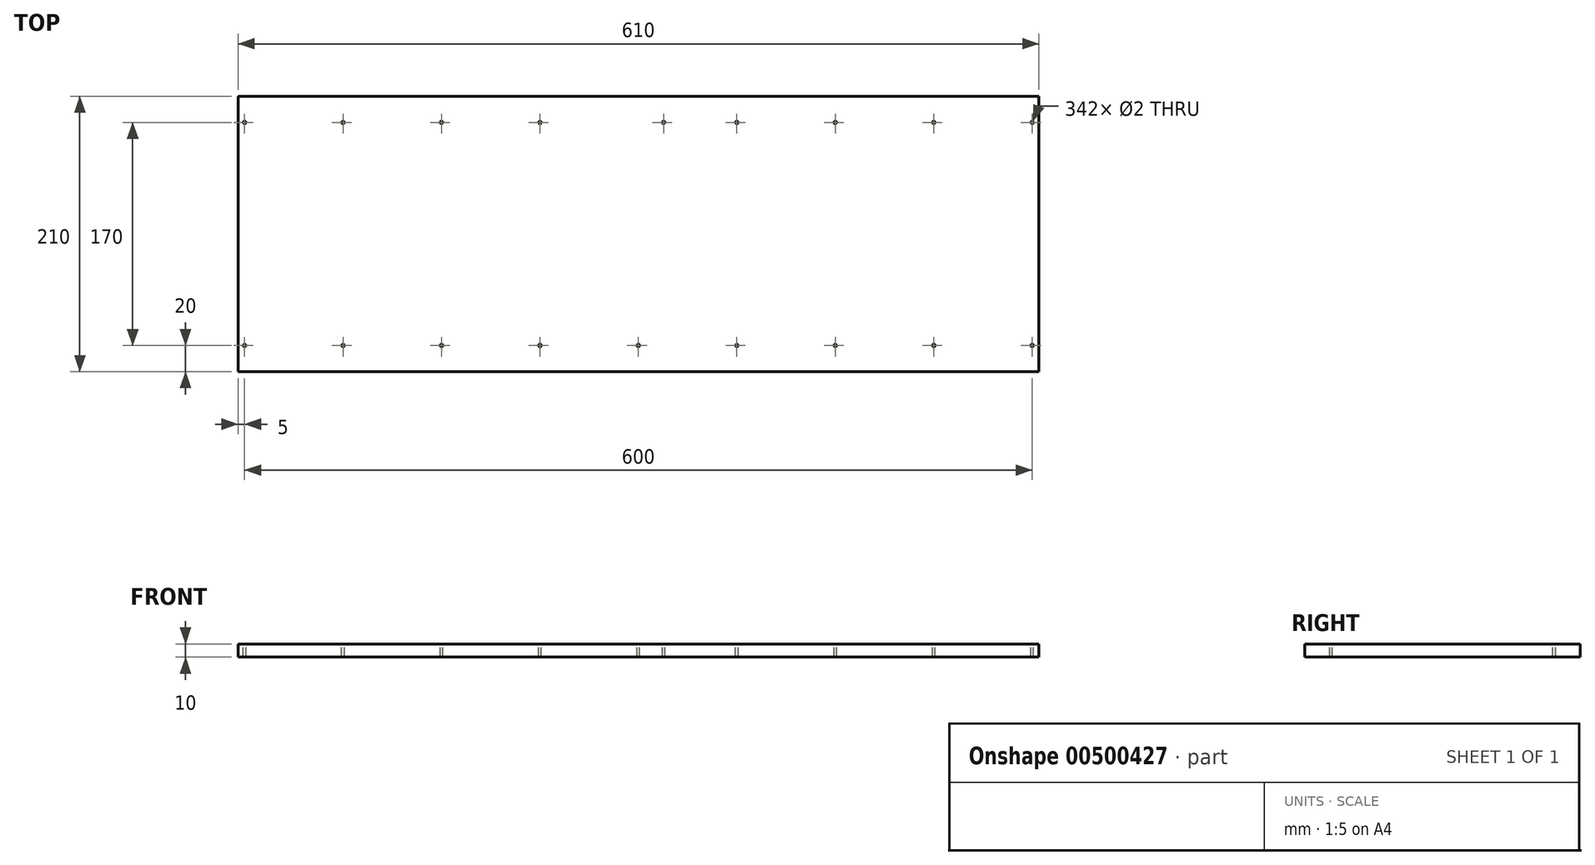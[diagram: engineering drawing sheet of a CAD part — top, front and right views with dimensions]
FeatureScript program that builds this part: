
annotation { "Feature Type Name" : "Feature", "Feature Type Description" : "" }
export const myFeature = defineFeature(function(context is Context, id is Id, definition is map)
    precondition{}
    {
        {
            var Q0;
            Q0=qCreatedBy(makeId("Top.planeOp"),FACE);
            var sketch = newSketch(context, id + "F0", { "sketchPlane" : qUnion([Q0])});
            skLineSegment(sketch, "E0.bottom", {"start": v(0, 0) * mm, "end": v(-610, 0) * mm});
            skLineSegment(sketch, "E0.top", {"start": v(0, -210) * mm, "end": v(-610, -210) * mm});
            skLineSegment(sketch, "E0.left", {"start": v(0, 0) * mm, "end": v(0, -210) * mm});
            skLineSegment(sketch, "E0.right", {"start": v(-610, 0) * mm, "end": v(-610, -210) * mm});
            skSolve(sketch);
        }
        {
            var Q0;
            Q0=makeQuery(id+"F0.imprint","IMPRINT",FACE,{"disambiguationData":[TD([[makeQuery(id+"F0.imprint","IMPRINT",EDGE,{"derivedFrom":sQuery(id+"F0.wireOp",EDGE,"E0.bottom")}),1.0]])]});
            extrude(context, id + "F1", {"entities" : qUnion([Q0]), "depth" : 10 * mm});
        }
        {
            var Q0;
            Q0=makeQuery(id+"F1.opExtrude","CAP_FACE",FACE,{"disambiguationData":[OSD([sQuery(id+"F0.wireOp",EDGE,"E0.bottom"),sQuery(id+"F0.wireOp",EDGE,"E0.top"),sQuery(id+"F0.wireOp",EDGE,"E0.left"),sQuery(id+"F0.wireOp",EDGE,"E0.right")])],"isStart":false});
            var sketch = newSketch(context, id + "F2", { "sketchPlane" : qUnion([Q0])});
            skPoint(sketch, "E1", {"position": v(-530, -190) * mm});
            skPoint(sketch, "E2", {"position": v(-455, -190) * mm});
            skPoint(sketch, "E3", {"position": v(-380, -190) * mm});
            skPoint(sketch, "E4", {"position": v(-305, -190) * mm});
            skPoint(sketch, "E5", {"position": v(-230, -190) * mm});
            skPoint(sketch, "E6", {"position": v(-155, -190) * mm});
            skPoint(sketch, "E7", {"position": v(-80, -190) * mm});
            skPoint(sketch, "E8", {"position": v(-530, -20) * mm});
            skPoint(sketch, "E9", {"position": v(-455, -20) * mm});
            skPoint(sketch, "E10", {"position": v(-380, -20) * mm});
            skPoint(sketch, "E11", {"position": v(-285.75, -20) * mm});
            skPoint(sketch, "E12", {"position": v(-230, -20) * mm});
            skPoint(sketch, "E13", {"position": v(-155, -20) * mm});
            skPoint(sketch, "E14", {"position": v(-80, -20) * mm});
            skPoint(sketch, "E15", {"position": v(-5, -190) * mm});
            skPoint(sketch, "E16", {"position": v(-5, -20) * mm});
            skPoint(sketch, "E17", {"position": v(-605, -20) * mm});
            skPoint(sketch, "E18", {"position": v(-605, -190) * mm});
            skSolve(sketch);
        }
        {
            var Q0;
            Q0=sQuery(id+"F2.wireOp",VERTEX,"E1");
            var Q1;
            Q1=sQuery(id+"F2.wireOp",VERTEX,"E2");
            var Q2;
            Q2=sQuery(id+"F2.wireOp",VERTEX,"E3");
            var Q3;
            Q3=sQuery(id+"F2.wireOp",VERTEX,"E4");
            var Q4;
            Q4=sQuery(id+"F2.wireOp",VERTEX,"E5");
            var Q5;
            Q5=sQuery(id+"F2.wireOp",VERTEX,"E6");
            var Q6;
            Q6=sQuery(id+"F2.wireOp",VERTEX,"E7");
            var Q7;
            Q7=sQuery(id+"F2.wireOp",VERTEX,"E14");
            var Q8;
            Q8=sQuery(id+"F2.wireOp",VERTEX,"E13");
            var Q9;
            Q9=sQuery(id+"F2.wireOp",VERTEX,"E12");
            var Q10;
            Q10=sQuery(id+"F2.wireOp",VERTEX,"E11");
            var Q11;
            Q11=sQuery(id+"F2.wireOp",VERTEX,"E10");
            var Q12;
            Q12=sQuery(id+"F2.wireOp",VERTEX,"E9");
            var Q13;
            Q13=sQuery(id+"F2.wireOp",VERTEX,"E8");
            var Q14;
            Q14=sQuery(id+"F2.wireOp",VERTEX,"E17");
            var Q15;
            Q15=sQuery(id+"F2.wireOp",VERTEX,"E18");
            var Q16;
            Q16=sQuery(id+"F2.wireOp",VERTEX,"E16");
            var Q17;
            Q17=sQuery(id+"F2.wireOp",VERTEX,"E15");
            var Q18;
            Q18=makeQuery(id+"F1.opExtrude","SWEPT_BODY",BODY,{"disambiguationData":[OSD([sQuery(id+"F0.wireOp",EDGE,"E0.bottom"),sQuery(id+"F0.wireOp",EDGE,"E0.top"),sQuery(id+"F0.wireOp",EDGE,"E0.left"),sQuery(id+"F0.wireOp",EDGE,"E0.right")])]});
            hole(context, id + "F3", {"style" : HoleStyle.SIMPLE, "endStyle" : HoleEndStyle.THROUGH, "holeDiameter" : 2 * mm, "isTappedThrough" : true, "tappedDepth" : 12 * mm, "tapClearance" : 3, "locations" : qUnion([Q0, Q1, Q2, Q3, Q4, Q5, Q6, Q7, Q8, Q9, Q10, Q11, Q12, Q13, Q14, Q15, Q16, Q17]), "scope" : qUnion([Q18])});
        }
    });
